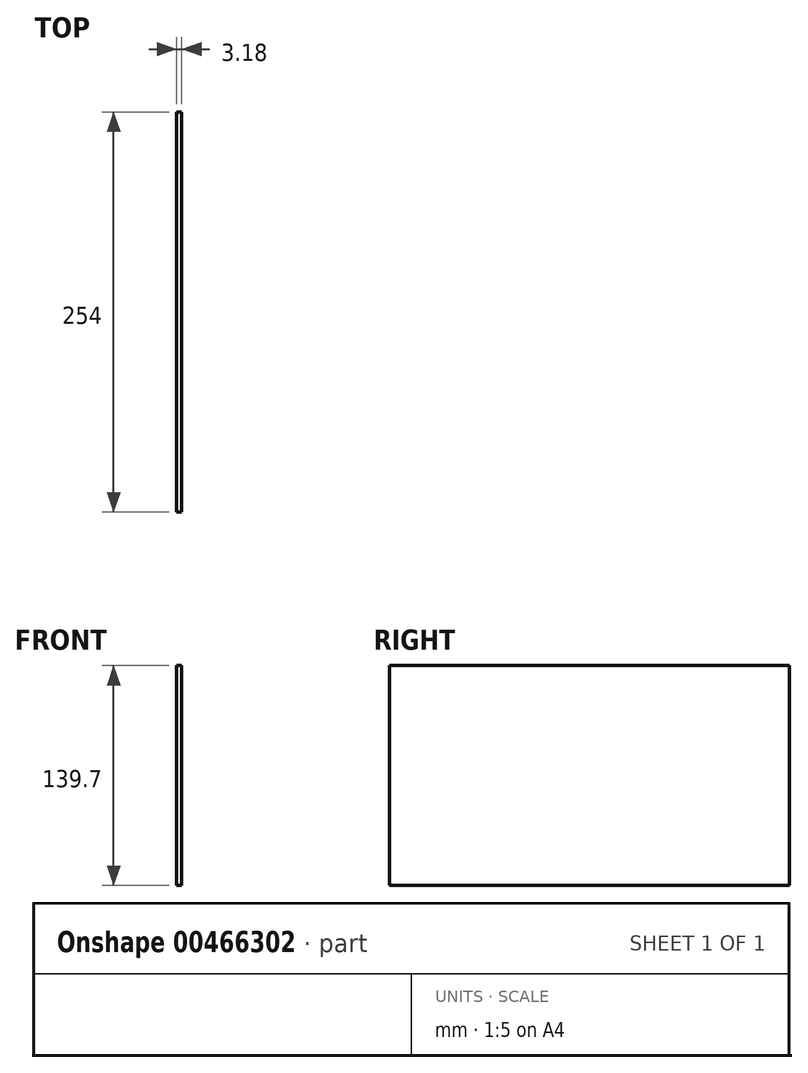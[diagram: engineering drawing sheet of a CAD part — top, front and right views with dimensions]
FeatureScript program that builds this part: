
annotation { "Feature Type Name" : "Feature", "Feature Type Description" : "" }
export const myFeature = defineFeature(function(context is Context, id is Id, definition is map)
    precondition{}
    {
        {
            var Q0;
            Q0=qCreatedBy(makeId("Front.planeOp"),FACE);
            var sketch = newSketch(context, id + "F0", { "sketchPlane" : qUnion([Q0])});
            skLineSegment(sketch, "E0", {"start": v(-45.8, 77.77) * mm, "end": v(-45.8, -61.93) * mm});
            skLineSegment(sketch, "E1", {"start": v(-45.8, -61.93) * mm, "end": v(-48.97, -61.93) * mm});
            skLineSegment(sketch, "E2", {"start": v(-48.97, 77.77) * mm, "end": v(-48.97, -61.93) * mm});
            skLineSegment(sketch, "E3", {"start": v(-45.8, 77.77) * mm, "end": v(-48.97, 77.77) * mm});
            skSolve(sketch);
        }
        {
            var Q0;
            Q0=makeQuery(id+"F0.imprint","IMPRINT",FACE,{"disambiguationData":[TD([[makeQuery(id+"F0.imprint","IMPRINT",EDGE,{"derivedFrom":sQuery(id+"F0.wireOp",EDGE,"E0")}),-1.0]])]});
            extrude(context, id + "F1", {"entities" : qUnion([Q0]), "depth" : 419.1 * mm});
        }
        {
            var Q0;
            Q0=makeQuery(id+"F1.opExtrude","CAP_FACE",FACE,{"disambiguationData":[OSD([sQuery(id+"F0.wireOp",EDGE,"E0"),sQuery(id+"F0.wireOp",EDGE,"E1"),sQuery(id+"F0.wireOp",EDGE,"E2"),sQuery(id+"F0.wireOp",EDGE,"E3")])],"isStart":true});
            extrude(context, id + "F2", {"entities" : qUnion([Q0]), "operationType" : NewBodyOperationType.REMOVE, "oppositeDirection" : true, "depth" : 165.1 * mm, "offsetDistance" : 25.4 * mm});
        }
    });
